# Revit family: Chair-Multi_Purpose-Allermuir-Quincy-QCY01
name_source: partatom
category: Furniture
revit_build: Autodesk Revit MEP 2012 (Build: 20110309_2315)
units: mm (PartAtom-declared; Revit-internal decimal feet)

## types (1)
- QCY01
    04 CSI = 12 51 00
    95 CSI = 12510
    Assembly Code = E2020200
    Base = Wood - Allermuir - Cherry - Light
    Color Availability = See price list for material options
    Cushion = Plastic - Allermuir - Smooth - Fine Textured - White
    Default Elevation = 48 "
    Description = Side chair with skid base
    Glide Finesh = Plastic - Allermuir - Smooth Black
    Glides = Plastic - Allermuir - Smooth Black
    Leg Material = Wood - Allermuir - Cherry - Light
    Manufacturer = Allermuir
    Manufacturer Fax = (419) 887 5805
    Model = QCY01
    Overall Depth = 20 "
    Overall Height = 32 "
    Overall Width = 18 "
    Plastic Arms in Black = No
    Plastic glides = Yes
    Product Line = Quincy
    Seat Depth = 18 "
    Seat Finesh = Plastic - Allermuir - Smooth - Fine Textured - White
    Seat Height = 17 "
    Seat Width = 18 "
    Seat or Top = Plastic - Allermuir - Smooth - Fine Textured - White
    Stacks = Yes
    Subcategory = Multi-Purpose
    Weight = 0.0 lb

## geometry (parser evidence)
native form markers: Blend x14, Sweep x1
no freeform markers — native parametric forms only
